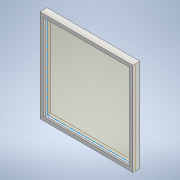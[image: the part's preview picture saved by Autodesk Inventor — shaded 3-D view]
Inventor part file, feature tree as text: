
AUTODESK INVENTOR PART (.ipt)
format: ipt  version: 2021 (Build 250183000, 183)  size: 152,064 bytes
history: native  units: mm
features: extrude x3, sketch x3, other x2, chamfer x1
ambient origin geometry x8: Origin, YZ Plane, XZ Plane, XY Plane, X Axis, Y Axis, Z Axis, Center Point
bodies: Body1 (feature_tree)
feature tree (9):
  other  "Bryła1"
  extrude  "Wyciągnięcie proste1"  Depth=1000.0mm
  extrude  "Wyciągnięcie proste2"  Depth=1000.0mm
  chamfer  "Faza1"  Distance=930.0mm
  other  "Płaszczyzna konstrukcyjna1"
  extrude  "Wyciągnięcie proste3"  Depth=930.0mm
  sketch  "Szkic1"
  sketch  "Szkic2"
  sketch  "Szkic3"
